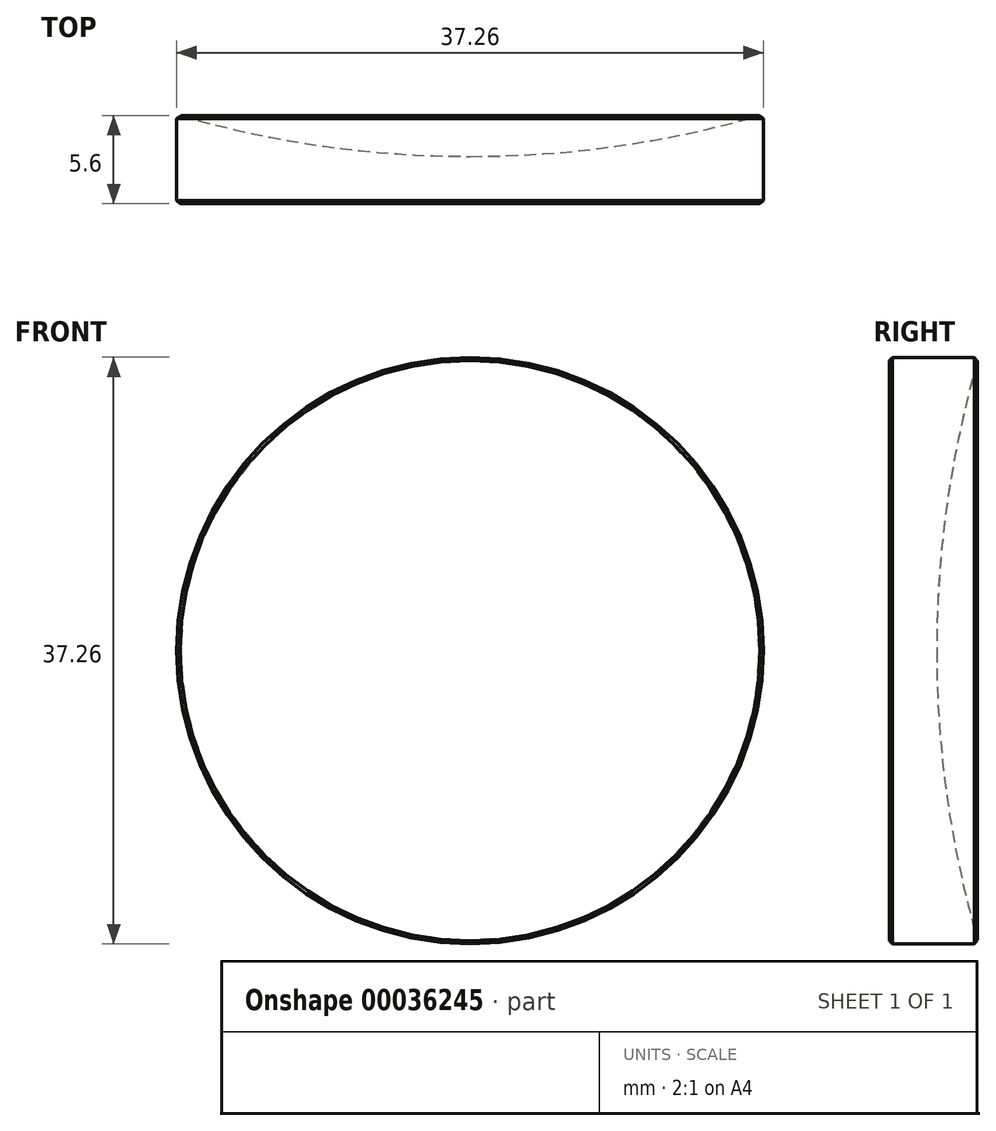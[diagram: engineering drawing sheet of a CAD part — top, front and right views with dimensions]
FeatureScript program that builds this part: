
annotation { "Feature Type Name" : "Feature", "Feature Type Description" : "" }
export const myFeature = defineFeature(function(context is Context, id is Id, definition is map)
    precondition{}
    {
        {
            var Q0;
            Q0=qCreatedBy(makeId("Right.planeOp"),FACE);
            var sketch = newSketch(context, id + "F0", { "sketchPlane" : qUnion([Q0])});
            skLineSegment(sketch, "E0", {"start": v(0, 0) * mm, "end": v(0, 18.62) * mm});
            skLineSegment(sketch, "E1", {"start": v(0, 18.62) * mm, "end": v(5.67, 18.62) * mm});
            skLineSegment(sketch, "E2", {"start": v(0, 0) * mm, "end": v(3, 0) * mm});
            skLineSegment(sketch, "E3", {"start": v(3, 0) * mm, "end": v(69.5, 0) * mm, "construction": true});
            skArc(sketch, "E4", {"start": v(5.67, 18.62) * mm, "mid": v(3.68, 9.4) * mm, "end": v(3, 0) * mm});
            skSolve(sketch);
        }
        {
            var Q0;
            Q0=makeQuery(id+"F0.imprint","IMPRINT",FACE,{"disambiguationData":[TD([[makeQuery(id+"F0.imprint","IMPRINT",EDGE,{"derivedFrom":sQuery(id+"F0.wireOp",EDGE,"E0")}),-1.0]])]});
            var Q1;
            Q1=sQuery(id+"F0.wireOp",EDGE,"E3");
            revolve(context, id + "F1", {"entities" : qUnion([Q0]), "axis" : qUnion([Q1]), "revolveType" : RevolveType.FULL});
        }
        {
            var Q0;
            Q0=makeQuery(id+"F1.opRevolve","SWEPT_EDGE",EDGE,{"disambiguationData":[OSD([sQuery(id+"F0.wireOp",EDGE,"E1"),sQuery(id+"F0.wireOp",EDGE,"E4")])]});
            var Q1;
            Q1=makeQuery(id+"F1.opRevolve","SWEPT_EDGE",EDGE,{"disambiguationData":[OSD([sQuery(id+"F0.wireOp",EDGE,"E0"),sQuery(id+"F0.wireOp",EDGE,"E1")])]});
            chamfer(context, id + "F2", {"entities" : qUnion([Q0, Q1]), "width" : .2 * mm, "tangentPropagation" : true});
        }
    });
